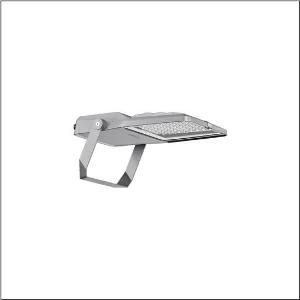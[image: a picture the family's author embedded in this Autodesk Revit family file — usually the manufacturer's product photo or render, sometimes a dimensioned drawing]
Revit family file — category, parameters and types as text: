
# Revit family: floodlight_fl_21_iq_mini___pl33t_5xa7772c5f1a_3dad
name_source: partatom
category: Lighting Fixtures
units: mm (PartAtom-declared; Revit-internal decimal feet)

## family parameters
Cut with Voids When Loaded = No
Host = Face
Light Source = No
Part Type = Normal
Room Calculation Point = No
Round Connector Dimension = Use Diameter
Shared = No

## types (1)
- --- (1 x LED, 11260 lm, 87.2 W, 4000K)
    Apparent Load = 87 VA
    CIE Flux Codes = 26 75 99 100 100
    Color Rendering = 80
    Color Temperature = 4000K
    Default Elevation = 1800 mm
    Description = Floodlight FL 21 iQ mini, floodlight, primary light control with lens, of PMMA, primary optical cover: protective disc, of toughened safety glass, transparent, light distribution: PL33T, light emission: direct distribution, installation type: surface-mounted, LED, High Power LED, rated luminous flux: 11.260lm, luminous efficacy: 129lm/W, light colour: 840, colour temperature: 4000K, control: Street-Remote, Auto-Match, Temp-Guard, Night-Set, Smart-Wire, Desk-Remote (wireless, voltage-free reading and setting of iQ features in the workshop via application-optimized NFC function/RFID function), optimised constant luminous flux control (CLO 2.0), with terminal, 6-pole, mains connection: 220..240V, AC, 50/60Hz, start of lifetime: 87W, end of service life: 92W, reduction: 40W, luminaire housing, of diecast aluminium, powder-coated, Siteco® metallic grey (DB 702S), corrosivity category C5 mid according to DIN EN ISO 12944, sealing non-destructively replaceable, mounting bracket, of steel, galvanised, powder-coated, Siteco® metallic grey (DB 702S), protection rating (complete): IP66, insulation class (complete): insulation class II (safety insulation), certification: CE, ENEC, VDE, protection symbol: D, impact resistance: IK08, permissible operating ambient temperature: -40..+40°C, permissible operating ambient temperature for outdoor applications: -40..+50°C, standard: DIN EN 12944, LABS conformity tested according to VDMA 24364:2018-05, packaging unit: 1 piece

Light Distribution: PL33T
    Height = 70 mm
    Lamp = 1 x LED
    Lamp Light Flux = 11260 lm
    Lamp Power = 87.2 W
    Lamp count = 1
    Length = 485 mm
    Luminous efficacy = 129 lm/W
    Manufacturer = Siteco
    ModVariant = No
    Model = 5XA7772C5F1A
    Number of Poles = 1
    OnlyDefault = Yes
    Power Factor = 1
    Product Name = Floodlight FL 21 iQ mini | PL33T
    Product group = floodlight | pylon annexe
    ProductGroupID = 6200
    Protection Class = Protection class II
    Protection Degree = IP 66
    RLX_Detail_Level = 1
    RLX_Emergency_Light_Flux = 0 lm
    RLX_Emergency_Type = 0
    RLX_Emergency_Type_DB = No
    RlxData = <blob elided: 96097 chars, md5=24ac2616>
    Socket = socket
    Standby Power = 0 W
    System Light Flux = 11260 lm
    System Power = 87 W
    Type Comments = factory setting: luminous flux: 100 % | dim-lin: 254 | 456 mA
    Type Image = l_1006845.jpg
    URL = http://relux.com
    VarID = @adj_081795
    Voltage = 0 V
    Weight = 0.00 kg
    Width = 337 mm

## geometry (parser evidence)
native form markers: Blend x4, Sweep x11
no freeform markers — native parametric forms only
